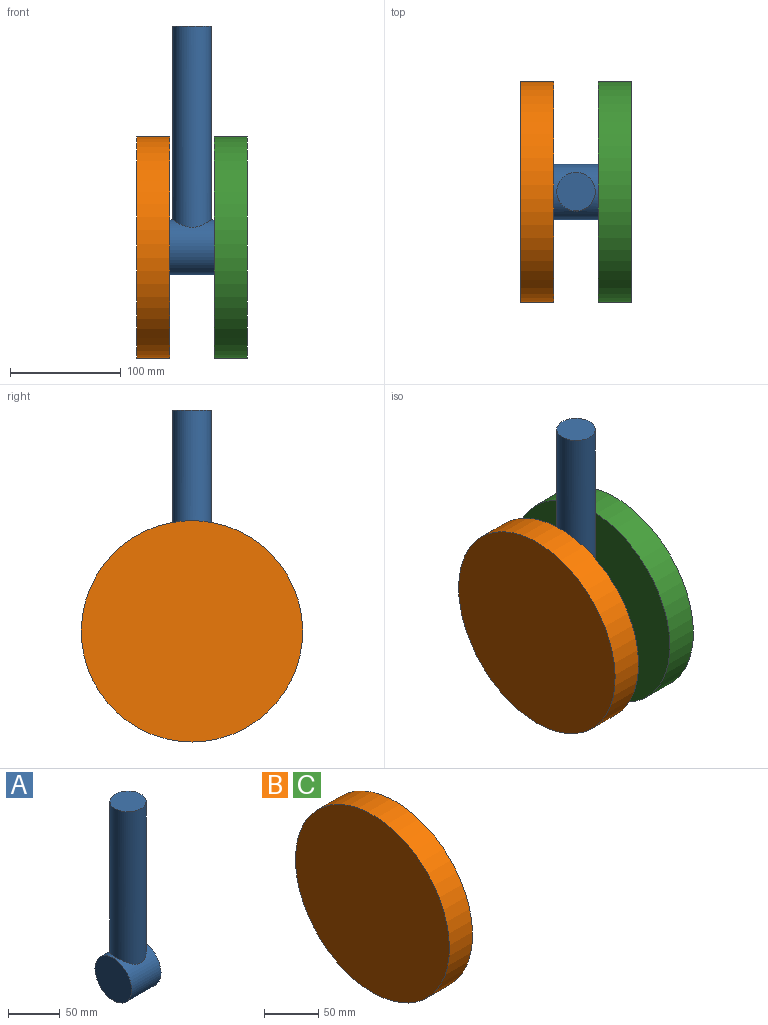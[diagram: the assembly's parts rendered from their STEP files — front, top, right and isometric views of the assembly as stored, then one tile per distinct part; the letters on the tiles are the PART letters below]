
ASSEMBLY  parts=3 mates=2
PART A: 5 faces, bbox 40x50x225 mm
  f0: cylinder r=25mm len=50mm, axis (-1,0,0), area 5261.6mm2, adj f1,f2,f3
  f1: plane 50x50mm, normal (1,0,0), area 1963.5mm2, adj f0
  f2: plane 50x50mm, normal (-1,0,0), area 1963.5mm2, adj f0
  f3: cylinder r=17.38mm len=182.03mm, axis (0,0,-1), area 19479mm2, adj f0,f4
  f4: plane 34.76x34.76mm, normal (0,0,1), area 949.1mm2, adj f3
PART B: 3 faces, bbox 30x200x200 mm
  f0: cylinder r=100mm len=200mm, axis (-1,0,0), area 18849.6mm2, adj f1,f2
  f1: plane 200x200mm, normal (1,0,0), area 31415.9mm2, adj f0
  f2: plane 200x200mm, normal (-1,0,0), area 31415.9mm2, adj f0
PART C: same geometry as B
PLACE A t=(75.25,32.91,-15.81)mm fixed
PLACE B t=(40.25,32.91,-15.81)mm
PLACE C t=(110.25,32.91,-15.81)mm
MATE revolute B.f0 <-> A.f0  axis (1,0,0) through (55.25,32.91,-15.81)mm
MATE revolute A.f0 <-> C.f0  axis (-1,0,0) through (95.25,32.91,-15.81)mm
